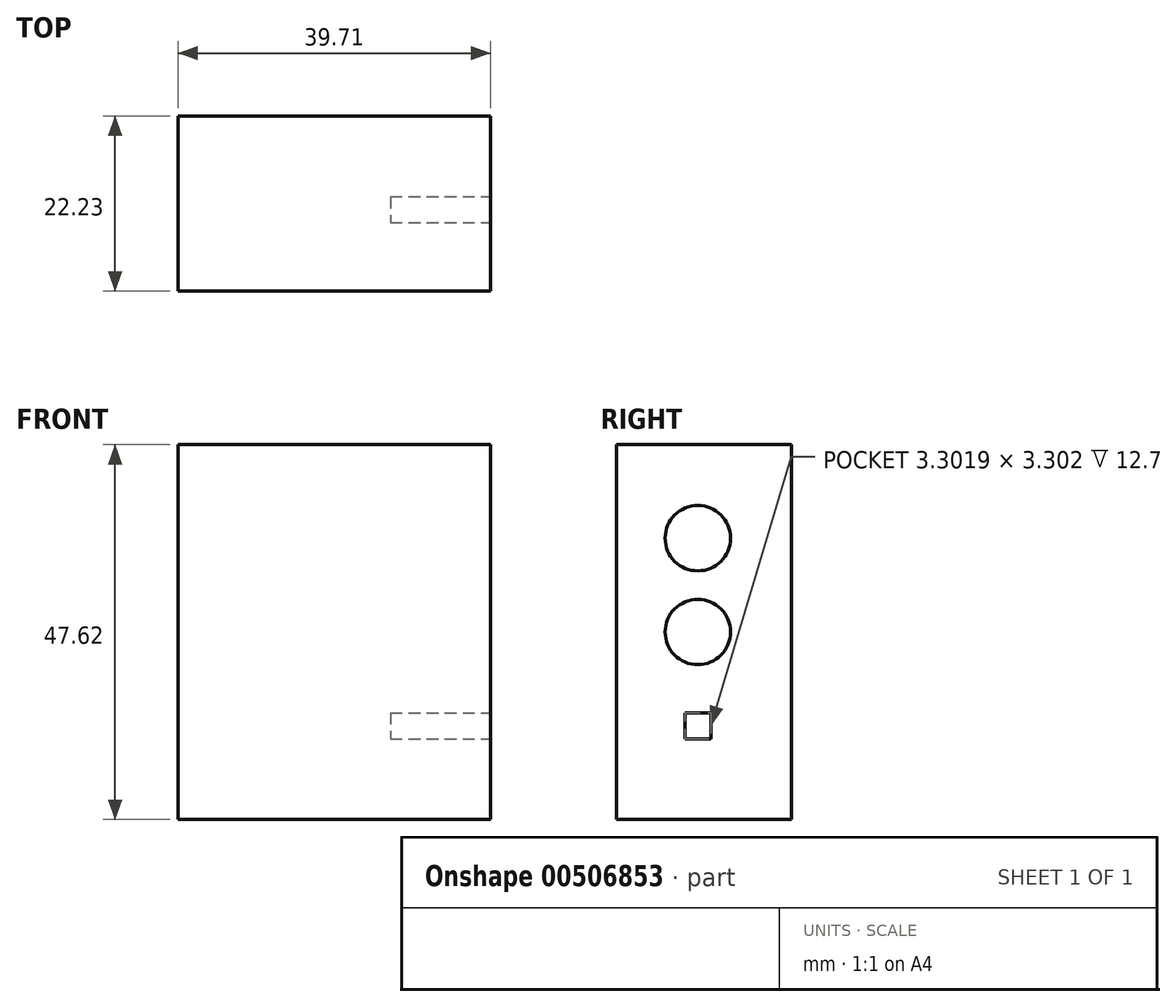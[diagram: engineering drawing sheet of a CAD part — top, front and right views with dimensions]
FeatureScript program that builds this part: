
annotation { "Feature Type Name" : "Feature", "Feature Type Description" : "" }
export const myFeature = defineFeature(function(context is Context, id is Id, definition is map)
    precondition{}
    {
        {
            var Q0;
            Q0=qCreatedBy(makeId("Front.planeOp"),FACE);
            var sketch = newSketch(context, id + "F0", { "sketchPlane" : qUnion([Q0])});
            skLineSegment(sketch, "E0.bottom", {"start": v(-23.47, 15.4) * mm, "end": v(16.21, 15.4) * mm});
            skLineSegment(sketch, "E0.top", {"start": v(-23.47, -32.23) * mm, "end": v(16.21, -32.23) * mm});
            skLineSegment(sketch, "E0.left", {"start": v(-23.47, 15.4) * mm, "end": v(-23.47, -32.23) * mm});
            skLineSegment(sketch, "E0.right", {"start": v(16.21, 15.4) * mm, "end": v(16.21, -32.23) * mm});
            skSolve(sketch);
        }
        {
            var Q0;
            Q0=makeQuery(id+"F0.imprint","IMPRINT",FACE,{"disambiguationData":[TD([[makeQuery(id+"F0.imprint","IMPRINT",EDGE,{"derivedFrom":sQuery(id+"F0.wireOp",EDGE,"E0.bottom")}),-1.0]])]});
            extrude(context, id + "F1", {"entities" : qUnion([Q0]), "depth" : 22.22 * mm, "offsetDistance" : 25.4 * mm});
        }
        {
            var Q0;
            Q0=makeQuery(id+"F1.opExtrude","SWEPT_FACE",FACE,{"disambiguationData":[OSD([sQuery(id+"F0.wireOp",EDGE,"E0.right")])]});
            var sketch = newSketch(context, id + "F2", { "sketchPlane" : qUnion([Q0])});
            skPoint(sketch, "E1", {"position": v(-11.9, -8.42) * mm});
            skPoint(sketch, "E2", {"position": v(-11.9, -20.33) * mm});
            skPoint(sketch, "E3", {"position": v(-11.9, 3.5) * mm});
            skCircle(sketch, "E4", {"center": v(-11.9, 3.5) * mm, "radius": 4.15 * mm});
            skCircle(sketch, "E5", {"center": v(-11.9, -8.42) * mm, "radius": 4.15 * mm});
            skLineSegment(sketch, "E6.bottom", {"start": v(-10.26, -18.68) * mm, "end": v(-13.56, -18.68) * mm});
            skLineSegment(sketch, "E6.top", {"start": v(-10.26, -21.98) * mm, "end": v(-13.56, -21.98) * mm});
            skLineSegment(sketch, "E6.left", {"start": v(-10.26, -18.68) * mm, "end": v(-10.26, -21.98) * mm});
            skLineSegment(sketch, "E6.right", {"start": v(-13.56, -18.68) * mm, "end": v(-13.56, -21.98) * mm});
            skSolve(sketch);
        }
        {
            var Q0;
            Q0=makeQuery(id+"F2.imprint","IMPRINT",FACE,{"disambiguationData":[TD([[makeQuery(id+"F2.imprint","IMPRINT",EDGE,{"derivedFrom":sQuery(id+"F2.wireOp",EDGE,"E4")}),1.0]])]});
            var Q1;
            Q1=makeQuery(id+"F2.imprint","IMPRINT",FACE,{"disambiguationData":[TD([[makeQuery(id+"F2.imprint","IMPRINT",EDGE,{"derivedFrom":sQuery(id+"F2.wireOp",EDGE,"E5")}),1.0]])]});
            extrude(context, id + "F3", {"entities" : qUnion([Q0, Q1]), "operationType" : NewBodyOperationType.ADD, "depth" : 5 / 203.2 * mm, "offsetDistance" : 25.4 * mm});
        }
        {
            var Q0;
            Q0=makeQuery(id+"F2.imprint","IMPRINT",FACE,{"disambiguationData":[TD([[makeQuery(id+"F2.imprint","IMPRINT",EDGE,{"derivedFrom":sQuery(id+"F2.wireOp",EDGE,"E6.bottom")}),1.0]])]});
            extrude(context, id + "F4", {"entities" : qUnion([Q0]), "operationType" : NewBodyOperationType.REMOVE, "oppositeDirection" : true, "depth" : 12.7 * mm, "offsetDistance" : 25.4 * mm});
        }
    });
